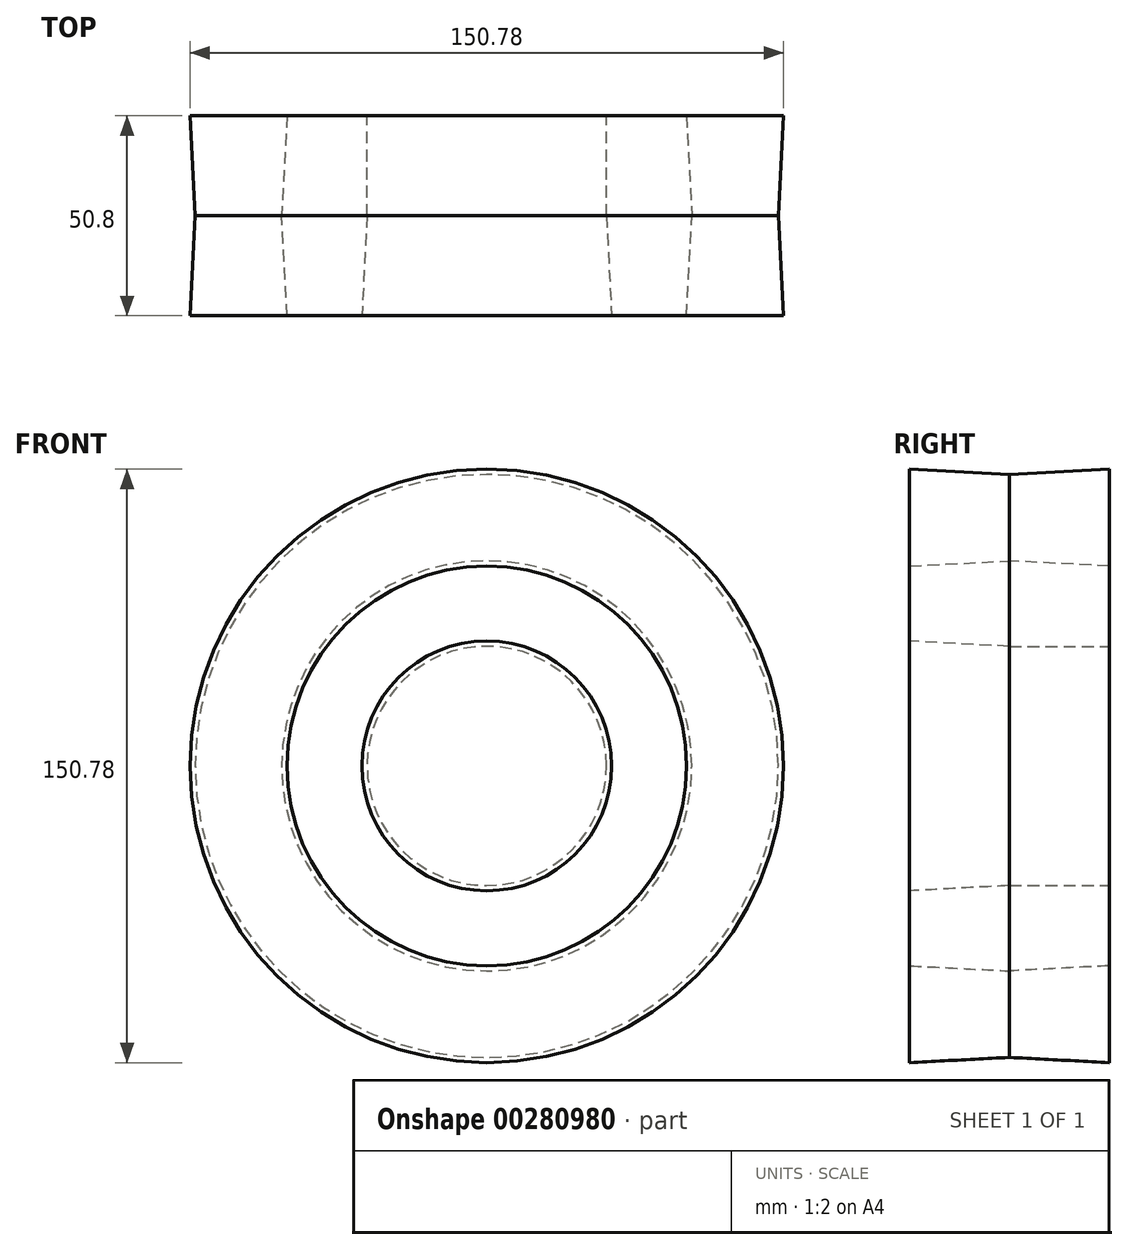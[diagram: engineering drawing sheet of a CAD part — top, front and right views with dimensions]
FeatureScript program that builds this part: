
annotation { "Feature Type Name" : "Feature", "Feature Type Description" : "" }
export const myFeature = defineFeature(function(context is Context, id is Id, definition is map)
    precondition{}
    {
        {
            var Q0;
            Q0=qCreatedBy(makeId("Front.planeOp"),FACE);
            var sketch = newSketch(context, id + "F0", { "sketchPlane" : qUnion([Q0])});
            skCircle(sketch, "E0", {"center": v(0, 0) * mm, "radius": 74.06 * mm});
            skCircle(sketch, "E1", {"center": v(0, 0) * mm, "radius": 52.1 * mm});
            skSolve(sketch);
        }
        {
            var Q0;
            Q0 = qSketchRegion(id + "F0", true);
            extrude(context, id + "F1", {"entities" : qUnion([Q0]), "depth" : 25.4 * mm, "hasDraft" : true, "draftAngle" : 3 * degree, "hasSecondDirection" : true, "secondDirectionOppositeDirection" : true, "secondDirectionDepth" : 25.4 * mm, "hasSecondDirectionDraft" : true, "secondDirectionDraftAngle" : 3 * degree});
        }
        {
            var Q0;
            Q0=qCreatedBy(makeId("Front.planeOp"),FACE);
            var sketch = newSketch(context, id + "F2", { "sketchPlane" : qUnion([Q0])});
            skCircle(sketch, "E2", {"center": v(-63.68, 0) * mm, "radius": 10.82 * mm});
            skCircle(sketch, "E3", {"center": v(0, 63.24) * mm, "radius": 10.82 * mm});
            skCircle(sketch, "E4", {"center": v(63.1, 0) * mm, "radius": 11.46 * mm});
            skCircle(sketch, "E5", {"center": v(0, -62.95) * mm, "radius": 11 * mm});
            skCircle(sketch, "E6", {"center": v(-49.27, 37.95) * mm, "radius": 10.82 * mm});
            skCircle(sketch, "E7", {"center": v(50.15, 39.42) * mm, "radius": 10.82 * mm});
            skCircle(sketch, "E8", {"center": v(-43.68, -45.89) * mm, "radius": 10.82 * mm});
            skCircle(sketch, "E9", {"center": v(45.45, -43.24) * mm, "radius": 10.82 * mm});
            skSolve(sketch);
        }
        {
            var Q0;
            Q0=sQuery(id+"F2.wireOp",EDGE,"E6");
            var Q1;
            Q1=sQuery(id+"F2.wireOp",EDGE,"E3");
            var Q2;
            Q2=sQuery(id+"F2.wireOp",EDGE,"E7");
            var Q3;
            Q3=sQuery(id+"F2.wireOp",EDGE,"E4");
            var Q4;
            Q4=sQuery(id+"F2.wireOp",EDGE,"E9");
            var Q5;
            Q5=sQuery(id+"F2.wireOp",EDGE,"E5");
            var Q6;
            Q6=sQuery(id+"F2.wireOp",EDGE,"E8");
            var Q7;
            Q7=sQuery(id+"F2.wireOp",EDGE,"E2");
            extrude(context, id + "F3", {"bodyType" : ToolBodyType.SURFACE, "operationType" : NewBodyOperationType.REMOVE, "surfaceEntities" : qUnion([Q0, Q1, Q2, Q3, Q4, Q5, Q6, Q7]), "depth" : 25.4 * mm, "hasDraft" : true, "draftAngle" : 3 * degree, "hasSecondDirection" : true, "secondDirectionOppositeDirection" : true, "secondDirectionDepth" : 25.4 * mm, "hasSecondDirectionDraft" : true, "secondDirectionDraftAngle" : 3 * degree});
        }
        {
            var Q0;
            Q0=qCreatedBy(makeId("Front.planeOp"),FACE);
            var sketch = newSketch(context, id + "F4", { "sketchPlane" : qUnion([Q0])});
            skCircle(sketch, "E10", {"center": v(0, 0) * mm, "radius": 30.4 * mm});
            skSolve(sketch);
        }
        {
            var Q0;
            Q0 = qSketchRegion(id + "F4", true);
            extrude(context, id + "F5", {"entities" : qUnion([Q0]), "depth" : 25.4 * mm, "hasDraft" : true, "draftAngle" : 3 * degree, "hasSecondDirection" : true, "secondDirectionOppositeDirection" : true, "secondDirectionDepth" : 25.4 * mm});
        }
    });
